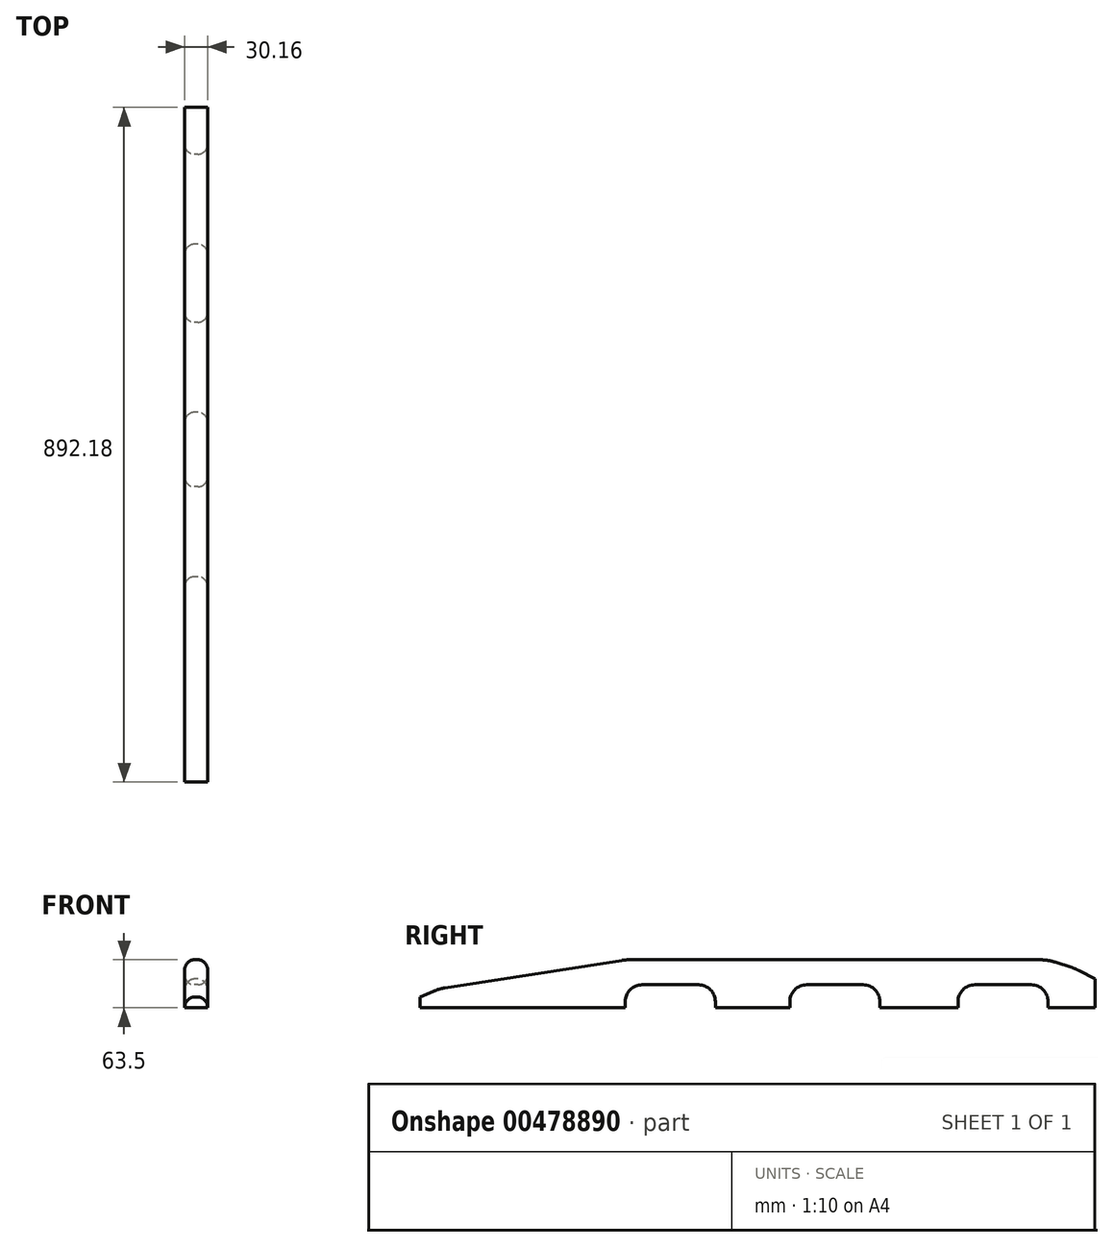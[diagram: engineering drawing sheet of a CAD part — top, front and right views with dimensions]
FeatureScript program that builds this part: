
annotation { "Feature Type Name" : "Feature", "Feature Type Description" : "" }
export const myFeature = defineFeature(function(context is Context, id is Id, definition is map)
    precondition{}
    {
        {
            var Q0;
            Q0=qCreatedBy(makeId("Right.planeOp"),FACE);
            var sketch = newSketch(context, id + "F0", { "sketchPlane" : qUnion([Q0])});
            skLineSegment(sketch, "E0.bottom", {"start": v(0, 0) * mm, "end": v(271.46, 0) * mm});
            skLineSegment(sketch, "E0.top", {"start": v(271.46, 63.5) * mm, "end": v(830.26, 63.5) * mm});
            skLineSegment(sketch, "E0.left", {"start": v(0, 0) * mm, "end": v(0, 14.29) * mm});
            skLineSegment(sketch, "E0.right", {"start": v(892.18, 0) * mm, "end": v(892.18, 38.1) * mm});
            skPoint(sketch, "E1", {"position": v(271.46, 0) * mm});
            skPoint(sketch, "E2", {"position": v(830.26, 0) * mm});
            skPoint(sketch, "E3", {"position": v(892.18, 38.1) * mm});
            skPoint(sketch, "E4", {"position": v(0, 14.29) * mm});
            skLineSegment(sketch, "E5", {"start": v(271.46, 0) * mm, "end": v(271.46, 30.48) * mm});
            skLineSegment(sketch, "E6", {"start": v(271.46, 30.48) * mm, "end": v(390.53, 30.48) * mm});
            skLineSegment(sketch, "E7", {"start": v(830.26, 30.48) * mm, "end": v(830.26, 0) * mm});
            skLineSegment(sketch, "E8.trimOffspring", {"start": v(830.26, 0) * mm, "end": v(892.18, 0) * mm});
            skLineSegment(sketch, "E9", {"start": v(0, 14.29) * mm, "end": v(25.4, 25.07) * mm});
            skLineSegment(sketch, "E10", {"start": v(25.4, 25.07) * mm, "end": v(271.46, 63.5) * mm});
            skLineSegment(sketch, "E11", {"start": v(892.18, 38.1) * mm, "end": v(866.78, 51.6) * mm});
            skLineSegment(sketch, "E12", {"start": v(866.78, 51.6) * mm, "end": v(830.26, 63.5) * mm});
            skLineSegment(sketch, "E13", {"start": v(390.53, 0) * mm, "end": v(488.95, 0) * mm});
            skLineSegment(sketch, "E14", {"start": v(711.2, 0) * mm, "end": v(711.2, 30.48) * mm});
            skLineSegment(sketch, "E15", {"start": v(608.01, 0) * mm, "end": v(608.01, 30.48) * mm});
            skLineSegment(sketch, "E16", {"start": v(488.95, 0) * mm, "end": v(488.95, 30.48) * mm});
            skLineSegment(sketch, "E17", {"start": v(390.53, 0) * mm, "end": v(390.53, 30.48) * mm});
            skLineSegment(sketch, "E18.trimOffspring", {"start": v(608.01, 0) * mm, "end": v(711.2, 0) * mm});
            skLineSegment(sketch, "E19.trimOffspring", {"start": v(711.2, 30.48) * mm, "end": v(830.26, 30.48) * mm});
            skLineSegment(sketch, "E20.trimOffspring", {"start": v(488.95, 30.48) * mm, "end": v(608.01, 30.48) * mm});
            skSolve(sketch);
        }
        {
            var Q0;
            Q0=makeQuery(id+"F0.imprint","IMPRINT",FACE,{"disambiguationData":[TD([[makeQuery(id+"F0.imprint","IMPRINT",EDGE,{"derivedFrom":sQuery(id+"F0.wireOp",EDGE,"E0.bottom")}),1.0]])]});
            extrude(context, id + "F1", {"entities" : qUnion([Q0]), "depth" : 15.08 * mm, "hasSecondDirection" : true, "secondDirectionOppositeDirection" : true, "secondDirectionDepth" : 15.08 * mm});
        }
        {
            var Q0;
            Q0=makeQuery(id+"F1.opExtrude","SWEPT_EDGE",EDGE,{"disambiguationData":[OSD([sQuery(id+"F0.wireOp",EDGE,"E9"),sQuery(id+"F0.wireOp",EDGE,"E10")])]});
            var Q1;
            Q1=makeQuery(id+"F1.opExtrude","SWEPT_EDGE",EDGE,{"disambiguationData":[OSD([sQuery(id+"F0.wireOp",EDGE,"E0.top"),sQuery(id+"F0.wireOp",EDGE,"E10")])]});
            var Q2;
            Q2=makeQuery(id+"F1.opExtrude","SWEPT_EDGE",EDGE,{"disambiguationData":[OSD([sQuery(id+"F0.wireOp",EDGE,"E0.top"),sQuery(id+"F0.wireOp",EDGE,"E12")])]});
            var Q3;
            Q3=makeQuery(id+"F1.opExtrude","SWEPT_EDGE",EDGE,{"disambiguationData":[OSD([sQuery(id+"F0.wireOp",EDGE,"E11"),sQuery(id+"F0.wireOp",EDGE,"E12")])]});
            fillet(context, id + "F2", {"entities" : qUnion([Q0, Q1, Q2, Q3]), "radius" : 63.5 * mm, "tangentPropagation" : true, "allowEdgeOverflow" : false});
        }
        {
            var Q0;
            Q0=makeQuery(id+"F1.opExtrude","SWEPT_EDGE",EDGE,{"disambiguationData":[OSD([sQuery(id+"F0.wireOp",EDGE,"E5"),sQuery(id+"F0.wireOp",EDGE,"E6")])]});
            var Q1;
            Q1=makeQuery(id+"F1.opExtrude","SWEPT_EDGE",EDGE,{"disambiguationData":[OSD([sQuery(id+"F0.wireOp",EDGE,"E16"),sQuery(id+"F0.wireOp",EDGE,"E20.trimOffspring")])]});
            var Q2;
            Q2=makeQuery(id+"F1.opExtrude","SWEPT_EDGE",EDGE,{"disambiguationData":[OSD([sQuery(id+"F0.wireOp",EDGE,"E14"),sQuery(id+"F0.wireOp",EDGE,"E19.trimOffspring")])]});
            var Q3;
            Q3=makeQuery(id+"F1.opExtrude","SWEPT_EDGE",EDGE,{"disambiguationData":[OSD([sQuery(id+"F0.wireOp",EDGE,"E6"),sQuery(id+"F0.wireOp",EDGE,"E17")])]});
            var Q4;
            Q4=makeQuery(id+"F1.opExtrude","SWEPT_EDGE",EDGE,{"disambiguationData":[OSD([sQuery(id+"F0.wireOp",EDGE,"E15"),sQuery(id+"F0.wireOp",EDGE,"E20.trimOffspring")])]});
            var Q5;
            Q5=makeQuery(id+"F1.opExtrude","SWEPT_EDGE",EDGE,{"disambiguationData":[OSD([sQuery(id+"F0.wireOp",EDGE,"E7"),sQuery(id+"F0.wireOp",EDGE,"E19.trimOffspring")])]});
            fillet(context, id + "F3", {"entities" : qUnion([Q0, Q1, Q2, Q3, Q4, Q5]), "radius" : 22.22 * mm, "tangentPropagation" : true, "allowEdgeOverflow" : false});
        }
        {
            var Q0;
            Q0=makeQuery(id+"F1.opExtrude","CAP_EDGE",EDGE,{"disambiguationData":[OSD([sQuery(id+"F0.wireOp",EDGE,"E6")])],"isStart":true});
            var Q1;
            Q1=makeQuery(id+"F1.opExtrude","CAP_EDGE",EDGE,{"disambiguationData":[OSD([sQuery(id+"F0.wireOp",EDGE,"E6")])],"isStart":false});
            var Q2;
            Q2=makeQuery(id+"F1.opExtrude","CAP_EDGE",EDGE,{"disambiguationData":[OSD([sQuery(id+"F0.wireOp",EDGE,"E20.trimOffspring")])],"isStart":true});
            var Q3;
            Q3=makeQuery(id+"F1.opExtrude","CAP_EDGE",EDGE,{"disambiguationData":[OSD([sQuery(id+"F0.wireOp",EDGE,"E20.trimOffspring")])],"isStart":false});
            var Q4;
            Q4=makeQuery(id+"F1.opExtrude","CAP_EDGE",EDGE,{"disambiguationData":[OSD([sQuery(id+"F0.wireOp",EDGE,"E19.trimOffspring")])],"isStart":true});
            var Q5;
            Q5=makeQuery(id+"F1.opExtrude","CAP_EDGE",EDGE,{"disambiguationData":[OSD([sQuery(id+"F0.wireOp",EDGE,"E19.trimOffspring")])],"isStart":false});
            var Q6;
            Q6=makeQuery(id+"F1.opExtrude","CAP_EDGE",EDGE,{"disambiguationData":[OSD([sQuery(id+"F0.wireOp",EDGE,"E0.top")])],"isStart":false});
            var Q7;
            Q7=makeQuery(id+"F1.opExtrude","CAP_EDGE",EDGE,{"disambiguationData":[OSD([sQuery(id+"F0.wireOp",EDGE,"E0.top")])],"isStart":true});
            fillet(context, id + "F4", {"entities" : qUnion([Q0, Q1, Q2, Q3, Q4, Q5, Q6, Q7]), "radius" : 12.7 * mm, "tangentPropagation" : true, "allowEdgeOverflow" : false});
        }
    });
